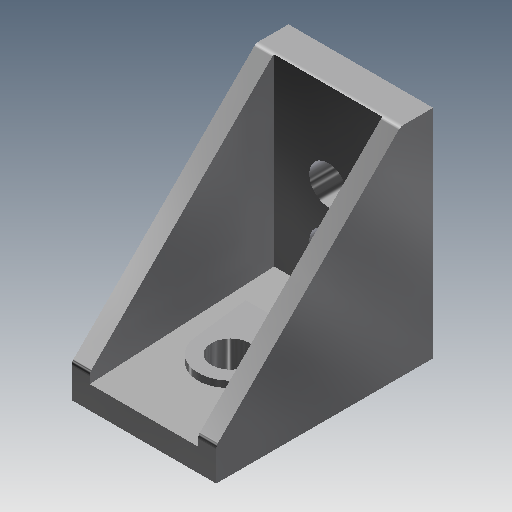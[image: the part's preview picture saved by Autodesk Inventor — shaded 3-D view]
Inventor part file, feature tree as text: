
AUTODESK INVENTOR PART (.ipt)
format: ipt  version: 2017 (Build 210142000, 142)  size: 247,296 bytes
history: native  units: mm
features: other x42, sketch x10, extrude x7, hole x3
ambient origin geometry x8: Origin, YZ Plane, XZ Plane, XY Plane, X Axis, Y Axis, Z Axis, Center Point
bodies: Solid1 (feature_tree)
feature tree (62):
  extrude  "Extrusion1"  Depth=15.0mm TaperAngle=0.0deg
  extrude  "Extrusion2"  Depth=1.0mm TaperAngle=0.0deg
  extrude  "Extrusion3"  Depth=1.0mm TaperAngle=0.0deg
  hole  "Hole1"  [1 undecoded]
  hole  "Hole2"  [1 undecoded]
  hole  "Hole3"  [1 undecoded]
  extrude  "Extrusion4"  [1 undecoded]
  extrude  "Extrusion5"  [1 undecoded]
  extrude  "Extrusion6"  [1 undecoded]
  extrude  "Extrusion7"  [1 undecoded]
  other  "bracket_to_bolt_XY"
  other  "bracket_to_bolt_YZ"
  other  "bracket_to_bolt_ZX"
  other  "bracket_to_bolt_X"
  other  "bracket_to_bolt_Y"
  other  "bracket_to_bolt_Z"
  other  "bracket_to_bolt_Center"
  other  "bracket_to_dummy_XY"
  other  "bracket_to_dummy_YZ"
  other  "bracket_to_dummy_ZX"
  other  "bracket_to_dummy_X"
  other  "bracket_to_dummy_Y"
  other  "bracket_to_dummy_Z"
  other  "bracket_to_dummy_Center"
  other  "to_bolt_4_7_base_XY"
  other  "to_bolt_4_7_base_YZ"
  other  "to_bolt_4_7_base_ZX"
  other  "to_bolt_4_7_base_X"
  other  "to_bolt_4_7_base_Y"
  other  "to_bolt_4_7_base_Z"
  other  "to_bolt_4_7_base_Center"
  other  "to_bolt_row_4_to_7_XY"
  other  "to_bolt_row_4_to_7_YZ"
  other  "to_bolt_row_4_to_7_ZX"
  other  "to_bolt_row_4_to_7_X"
  other  "to_bolt_row_4_to_7_Y"
  other  "to_bolt_row_4_to_7_Z"
  other  "to_bolt_row_4_to_7_Center"
  other  "to_nut_base_4_7_XY"
  other  "to_nut_base_4_7_YZ"
  other  "to_nut_base_4_7_ZX"
  other  "to_nut_base_4_7_X"
  other  "to_nut_base_4_7_Y"
  other  "to_nut_base_4_7_Z"
  other  "to_nut_base_4_7_Center"
  other  "to_nut_row_4_to_7_XY"
  other  "to_nut_row_4_to_7_YZ"
  other  "to_nut_row_4_to_7_ZX"
  other  "to_nut_row_4_to_7_X"
  other  "to_nut_row_4_to_7_Y"
  other  "to_nut_row_4_to_7_Z"
  other  "to_nut_row_4_to_7_Center"
  sketch  "Sketch_15"
  sketch  "Sketch_16"
  sketch  "Sketch_17"
  sketch  "Sketch4"  dims[d4=2.25mm d5=0.0mm]
  sketch  "Sketch5"  dims[d13=5.3mm d14=6.0mm d15=4.0mm d16=2.0mm d17=90.0deg d18=4.5mm d19=0.0mm]
  sketch  "Sketch6"  dims[d20=5.3mm d21=6.0mm d22=4.0mm d23=2.0mm d24=90.0deg d25=4.5mm d26=0.0mm d27=1.0mm d28=0.0mm]
  sketch  "Sketch_1"  dims[d0=20.0mm d1=0.0mm d2=15.0mm d3=0.0mm]
  sketch  "Sketch_4"  dims[d6=5.3mm d7=6.0mm d8=4.0mm d9=2.0mm d10=90.0deg d11=4.5mm d12=0.0mm]
  sketch  "Sketch_10"  dims[d29=1.0mm d30=0.0mm d31=1.0mm d32=0.0mm]
  sketch  "Sketch_11"  dims[d33=1.0mm d34=0.0mm]
note: 7 required parameter values undecoded (feature->parameter linkage not recoverable at this tier; creation-order binding heuristic only, values carry confidence <= 0.55)
